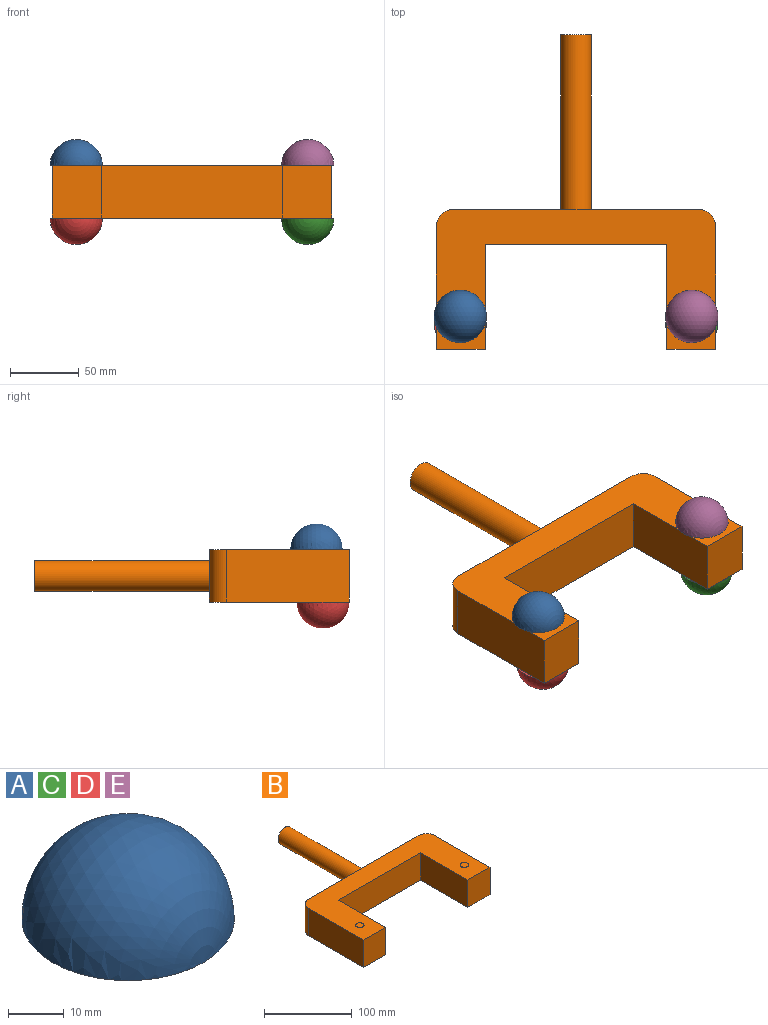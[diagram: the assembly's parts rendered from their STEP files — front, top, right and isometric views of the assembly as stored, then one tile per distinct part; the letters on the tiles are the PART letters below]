
ASSEMBLY  parts=5 mates=4
PART A: 2 faces, bbox 38.1x38.1x19.1 mm
  f0: sphere r=19.05mm, area 2280.2mm2, adj f1
  f1: plane 38.1x38.1mm, normal (0,0,-1), area 1140.1mm2, adj f0
PART B: 22 faces, bbox 203.2x228.6x38.6 mm
  f0: plane 88.9x38.1mm, normal (-1,0,0), area 3387.1mm2, adj f1,f9,f10,f11
  f1: plane 38.1x35.56mm, normal (0,-1,0), area 1354.8mm2, adj f0,f2,f10,f11
  f2: plane 76.2x38.1mm, normal (1,0,0), area 2903.2mm2, adj f1,f3,f10,f11
  f3: plane 132.08x38.1mm, normal (0,-1,0), area 5032.2mm2, adj f2,f4,f10,f11
  f4: plane 76.2x38.1mm, normal (-1,0,0), area 2903.2mm2, adj f3,f5,f10,f11
  f5: plane 38.1x35.56mm, normal (0,-1,0), area 1354.8mm2, adj f4,f6,f10,f11
  f6: plane 88.9x38.1mm, normal (1,0,0), area 3387.1mm2, adj f5,f7,f10,f11
  f7: cylinder r=12.7mm len=38.1mm, axis (0,0,-1), area 760.1mm2, adj f6,f8,f10,f11
  f8: plane 177.8x38.1mm, normal (0,1,0), area 6386.2mm2, adj f7,f9,f10,f11,f16
  f9: cylinder r=12.7mm len=38.1mm, axis (0,0,-1), area 760.1mm2, adj f0,f8,f10,f11
  f10: plane 203.2x101.6mm, normal (0,0,1), area 10368.9mm2, adj f0,f1,f2,f3,f4,f5,f6,f7
  f11: plane 203.2x101.6mm, normal (0,0,-1), area 10368.9mm2, adj f0,f1,f2,f3,f4,f5,f6,f7
  f12: cylinder r=4.76mm len=9.53mm, axis (0,0,-1), area 7.6mm2, adj f10,f13
  f13: plane 9.53x9.53mm, normal (0,0,1), area 71.3mm2, adj f12
  f14: cylinder r=4.76mm len=9.53mm, axis (0,0,-1), area 7.6mm2, adj f10,f15
  f15: plane 9.53x9.53mm, normal (0,0,1), area 71.3mm2, adj f14
  f16: cylinder r=11.11mm len=127mm, axis (0,-1,0), area 8867.4mm2, adj f8,f17
  f17: plane 22.23x22.23mm, normal (0,1,0), area 387.9mm2, adj f16
  f18: cylinder r=4.76mm len=9.53mm, axis (0,0,1), area 7.6mm2, adj f11,f19
  f19: plane 9.53x9.53mm, normal (0,0,-1), area 71.3mm2, adj f18
  f20: cylinder r=4.76mm len=9.53mm, axis (0,0,1), area 7.6mm2, adj f11,f21
  f21: plane 9.53x9.53mm, normal (0,0,-1), area 71.3mm2, adj f20
PART C: same geometry as A
PART D: same geometry as A
PART E: same geometry as A
PLACE A t=(-47.05,-28.92,79.29)mm
PLACE B t=(28.45,-9.86,41.19)mm
PLACE C rot(axis=(1,0,0),180deg) t=(121.23,-33.68,40.93)mm
PLACE D rot(axis=(1,0,0),180deg) t=(-47.05,-33.68,40.93)mm
PLACE E t=(121.23,-28.92,79.29)mm
MATE fastened A.f1 <-> B.f12  axis (0,0,-1) through (-47.05,-28.92,79.29)mm
MATE fastened E.f1 <-> B.f14  axis (0,0,-1) through (121.23,-28.92,79.29)mm
MATE fastened C.f1 <-> B.f20  axis (0,0,1) through (121.23,-33.68,40.93)mm
MATE fastened D.f1 <-> B.f18  axis (0,0,1) through (-47.05,-33.68,40.93)mm
